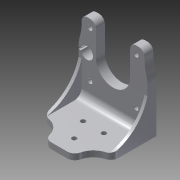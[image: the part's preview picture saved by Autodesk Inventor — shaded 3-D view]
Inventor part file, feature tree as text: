
AUTODESK INVENTOR PART (.ipt)
format: ipt  version: 2015 SP1 (Build 190203100, 203)  size: 318,976 bytes
history: native  units: mm
features: reference x13, sketch x12, extrude x11, fillet x6, projected_geometry x6, hole x4, mirror x1
ambient origin geometry x8: Origin, YZ Plane, XZ Plane, XY Plane, X Axis, Y Axis, Z Axis, Center Point
bodies: Solid2 (feature_tree)
feature tree (53):
  hole  "hole points"  [1 undecoded]
  extrude  "back plate Extrusion2"  Depth=4.0mm
  hole  "Hole3"  [1 undecoded]
  extrude  "Extrusion3"  Depth=8.0mm
  extrude  "Extrusion4"  Depth=4.0mm
  extrude  "Extrusion5"  Depth=42.3mm
  hole  "Hole4"  [1 undecoded]
  extrude  "Extrusion6"  Depth=10.0mm
  hole  "Hole5"  [1 undecoded]
  extrude  "Extrusion7"  Depth=1.0mm
  extrude  "Extrusion8"  Depth=6.0mm
  extrude  "Extrusion9"  Depth=5.0mm TaperAngle=0.0deg
  fillet  "Fillet3"  Radius=3.3mm
  fillet  "Fillet6"  Radius=5.0mm
  extrude  "Extrusion12"  Depth=4.0mm
  extrude  "Extrusion13"  Depth=5.0mm
  fillet  "Fillet10"  Radius=30.0mm
  fillet  "Fillet11"  Radius=2.0mm
  extrude  "Extrusion14"  Depth=2.0mm TaperAngle=0.0deg
  fillet  "Fillet14"  Radius=12.0mm
  fillet  "Fillet15"  Radius=5.0mm
  mirror  "Mirror1"
  sketch  "Sketch4"  dims[d0=14.0mm d1=13.0mm]
  reference  "Reference1"
  sketch  "Sketch5"  dims[d21=4.0mm d22=0.0mm d31=18.0mm]
  reference  "Reference2"
  sketch  "Sketch6"  dims[d32=4.0mm d33=4.0mm]
  reference  "Reference3"
  reference  "Reference4"
  reference  "Reference5"
  reference  "Reference6"
  reference  "Reference7"
  sketch  "Sketch7"  dims[d34=17.0mm d35=8.0mm]
  reference  "Reference8"
  reference  "Reference9"
  reference  "Reference10"
  reference  "Reference11"
  sketch  "Sketch8"  dims[d36=8.0mm]
  reference  "Reference12"
  sketch  "Sketch9"  dims[d37=3.2mm d38=6.0mm d39=4.0mm d40=2.0mm d41=90.0deg d42=8.0mm d43=20.594885mm d44=4.0mm]
  reference  "Reference13"
  sketch  "Sketch10"  dims[d45=10.0mm d46=0.0mm d47=42.3mm]
  projected_geometry  "Projected Loop1"
  sketch  "Sketch11"  dims[d48=48.0mm d49=0.0mm d50=1.0mm]
  projected_geometry  "Projected Loop2"
  sketch  "Sketch12"  dims[d53=50.0mm d54=0.0mm]
  projected_geometry  "Projected Loop3"
  sketch  "Sketch15"  dims[d55=3.2mm d56=6.0mm d57=4.0mm d58=2.0mm d59=90.0deg d60=8.0mm d61=20.594885mm d62=10.0mm]
  projected_geometry  "Projected Loop4"
  sketch  "Sketch16"  dims[d63=6.0mm d64=2.0mm d65=0.0mm]
  projected_geometry  "Projected Loop5"
  sketch  "Sketch17"  dims[d66=17.5mm d67=8.0mm d68=6.0mm d69=4.0mm d70=2.0mm d71=90.0deg d72=8.0mm d73=20.594885mm d74=1.0mm d75=6.0mm d76=5.0mm d77=0.0mm d78=3.3mm d79=0.0mm d80=5.0mm d81=0.0mm d93=4.0mm d96=5.0mm d97=30.0mm d98=2.0mm d99=0.0mm d100=2.0mm d101=0.0mm d105=12.0mm d106=5.0mm d109=5.5mm d110=0.0mm d111=25.0mm d112=20.0mm]
  projected_geometry  "Projected Loop6"
note: 4 required parameter values undecoded (feature->parameter linkage not recoverable at this tier; creation-order binding heuristic only, values carry confidence <= 0.55)
